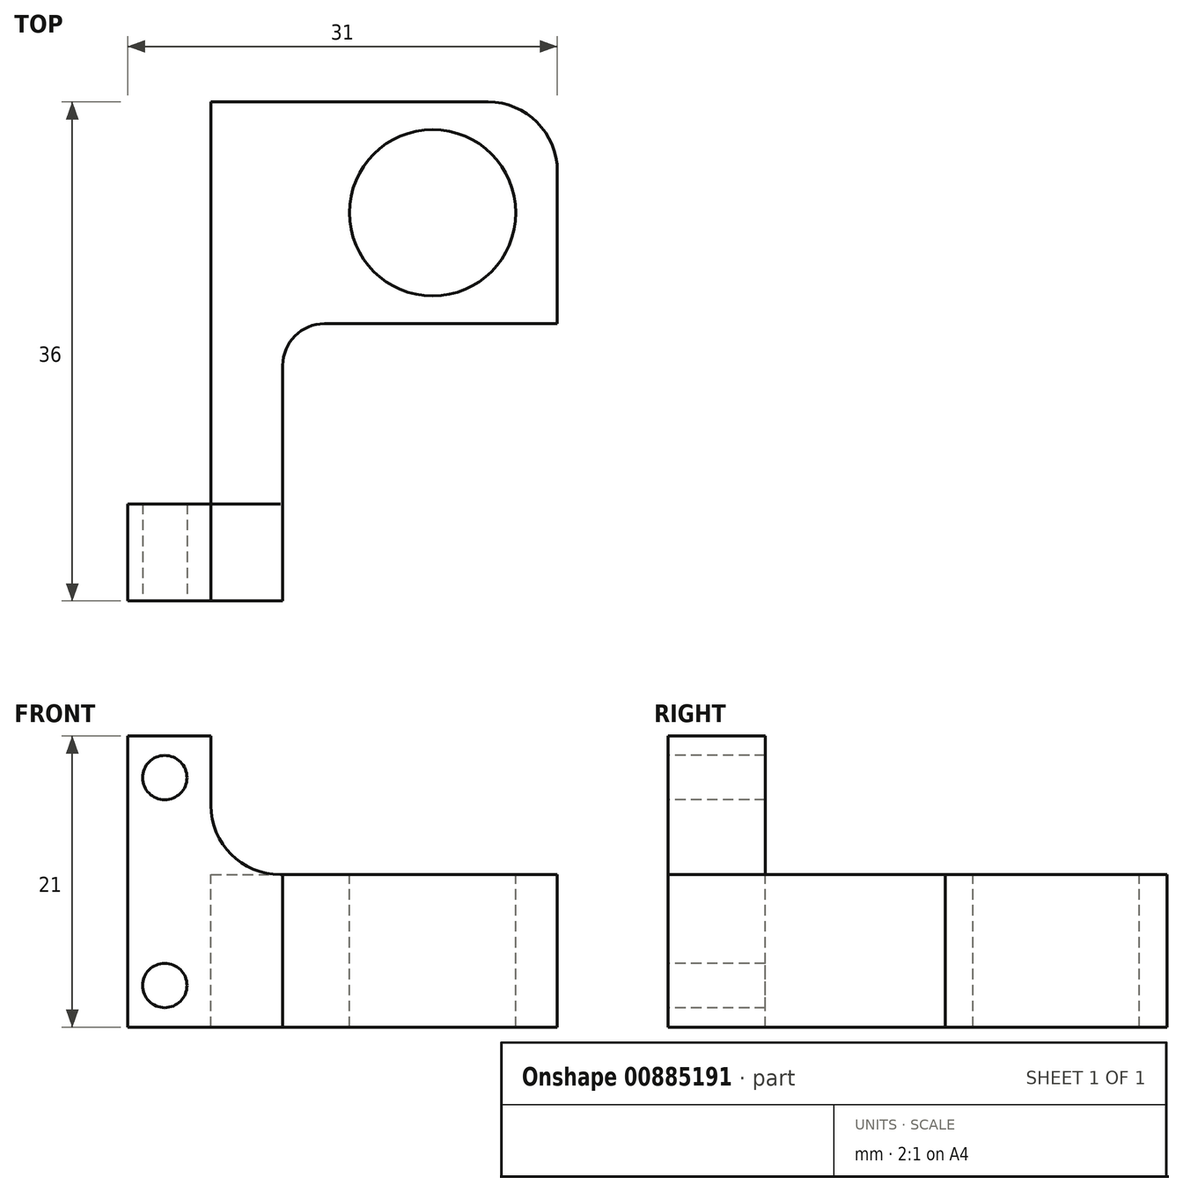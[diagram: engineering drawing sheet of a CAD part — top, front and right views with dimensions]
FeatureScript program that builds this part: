
annotation { "Feature Type Name" : "Feature", "Feature Type Description" : "" }
export const myFeature = defineFeature(function(context is Context, id is Id, definition is map)
    precondition{}
    {
        {
            var Q0;
            Q0=qCreatedBy(makeId("Top.planeOp"),FACE);
            var sketch = newSketch(context, id + "F0", { "sketchPlane" : qUnion([Q0])});
            skLineSegment(sketch, "E0.bottom", {"start": v(0, 0) * mm, "end": v(31, 0) * mm});
            skLineSegment(sketch, "E0.top", {"start": v(0, 36) * mm, "end": v(31, 36) * mm});
            skLineSegment(sketch, "E0.left", {"start": v(0, 0) * mm, "end": v(0, 36) * mm});
            skLineSegment(sketch, "E0.right", {"start": v(31, 0) * mm, "end": v(31, 36) * mm});
            skSolve(sketch);
        }
        {
            var Q0;
            Q0=qSketchRegion(id+"F0",true);
            extrude(context, id + "F1", {"entities" : qUnion([Q0]), "depth" : 4 * mm});
        }
        {
            var Q0;
            Q0=makeQuery(id+"F1.opExtrude","CAP_FACE",FACE,{"disambiguationData":[OSD([sQuery(id+"F0.wireOp",EDGE,"E0.bottom"),sQuery(id+"F0.wireOp",EDGE,"E0.top"),sQuery(id+"F0.wireOp",EDGE,"E0.left"),sQuery(id+"F0.wireOp",EDGE,"E0.right")])],"isStart":false});
            var sketch = newSketch(context, id + "F2", { "sketchPlane" : qUnion([Q0])});
            skCircle(sketch, "E1", {"center": v(22, 28) * mm, "radius": 6 * mm});
            skLineSegment(sketch, "E2.bottom", {"start": v(0, 36) * mm, "end": v(6, 36) * mm});
            skLineSegment(sketch, "E2.top", {"start": v(0, 7) * mm, "end": v(6, 7) * mm});
            skLineSegment(sketch, "E2.left", {"start": v(0, 36) * mm, "end": v(0, 7) * mm});
            skLineSegment(sketch, "E2.right", {"start": v(6, 36) * mm, "end": v(6, 7) * mm});
            skLineSegment(sketch, "E3.bottom", {"start": v(31, 0) * mm, "end": v(11.18, 0) * mm});
            skLineSegment(sketch, "E3.top", {"start": v(31, 20) * mm, "end": v(11.18, 20) * mm});
            skLineSegment(sketch, "E3.left", {"start": v(31, 0) * mm, "end": v(31, 20) * mm});
            skLineSegment(sketch, "E3.right", {"start": v(11.18, 0) * mm, "end": v(11.18, 20) * mm});
            skSolve(sketch);
        }
        {
            var Q0;
            Q0=qSketchRegion(id+"F2",true);
            extrude(context, id + "F3", {"entities" : qUnion([Q0]), "operationType" : NewBodyOperationType.REMOVE, "oppositeDirection" : true, "depth" : 25 * mm, "offsetDistance" : 25 * mm});
        }
        {
            var Q0;
            Q0=makeQuery(id+"F1.opExtrude","CAP_FACE",FACE,{"disambiguationData":[OSD([sQuery(id+"F0.wireOp",EDGE,"E0.bottom"),sQuery(id+"F0.wireOp",EDGE,"E0.top"),sQuery(id+"F0.wireOp",EDGE,"E0.left"),sQuery(id+"F0.wireOp",EDGE,"E0.right")])],"isStart":false});
            var sketch = newSketch(context, id + "F4", { "sketchPlane" : qUnion([Q0])});
            skLineSegment(sketch, "E4.bottom", {"start": v(0, 7) * mm, "end": v(6, 7) * mm});
            skLineSegment(sketch, "E4.top", {"start": v(0, 0) * mm, "end": v(6, 0) * mm});
            skLineSegment(sketch, "E4.left", {"start": v(0, 7) * mm, "end": v(0, 0) * mm});
            skLineSegment(sketch, "E4.right", {"start": v(6, 7) * mm, "end": v(6, 0) * mm});
            skSolve(sketch);
        }
        {
            var Q0;
            Q0=qSketchRegion(id+"F4",true);
            var Q1;
            {var subQ1=sQuery(id+"F4.wireOp",EDGE,"E4.right");Q1=makeQuery(id+"F4.imprint","IMPRINT",FACE,{"disambiguationData":[TD([[makeQuery(id+"F4.imprint","IMPRINT",EDGE,{"derivedFrom":subQ1}),1.0]])]});}
            extrude(context, id + "F5", {"entities" : qUnion([Q0, Q1]), "operationType" : NewBodyOperationType.ADD, "depth" : 7 * mm, "offsetDistance" : 25 * mm});
        }
        {
            var Q0;
            Q0=makeQuery(id+"F4.imprint","IMPRINT",FACE,{"disambiguationData":[TD([[makeQuery(id+"F4.imprint","IMPRINT",EDGE,{"derivedFrom":sQuery(id+"F4.wireOp",EDGE,"E4.bottom")}),-1.0]])]});
            extrude(context, id + "F6", {"entities" : qUnion([Q0]), "operationType" : NewBodyOperationType.ADD, "depth" : 17 * mm});
        }
        {
            var Q0;
            Q0=makeQuery(id+"F5.boolean.opBoolean","MERGE",FACE,{"derivedFrom":[makeQuery(id+"F1.opExtrude","SWEPT_FACE",FACE,{"disambiguationData":[OSD([sQuery(id+"F0.wireOp",EDGE,"E0.bottom")])]}),makeQuery(id+"F5.opExtrude","SWEPT_FACE",FACE,{"disambiguationData":[OSD([sQuery(id+"F4.wireOp",EDGE,"E4.top")])]})]});
            var sketch = newSketch(context, id + "F7", { "sketchPlane" : qUnion([Q0])});
            skLineSegment(sketch, "E5", {"start": v(2.68, 18) * mm, "end": v(2.68, 3) * mm});
            skCircle(sketch, "E6", {"center": v(2.68, 18) * mm, "radius": 1.6 * mm});
            skCircle(sketch, "E7", {"center": v(2.68, 3) * mm, "radius": 1.6 * mm});
            skSolve(sketch);
        }
        {
            var Q0;
            Q0=qSketchRegion(id+"F7",true);
            extrude(context, id + "F8", {"entities" : qUnion([Q0]), "operationType" : NewBodyOperationType.REMOVE, "oppositeDirection" : true, "depth" : 25 * mm});
        }
        {
            var Q0;
            Q0=makeQuery(id+"F1.opExtrude","SWEPT_EDGE",EDGE,{"disambiguationData":[OSD([sQuery(id+"F0.wireOp",EDGE,"E0.bottom"),sQuery(id+"F0.wireOp",EDGE,"E0.right")])]});
            var Q1;
            Q1=makeQuery(id+"F1.opExtrude","SWEPT_EDGE",EDGE,{"disambiguationData":[OSD([sQuery(id+"F0.wireOp",EDGE,"E0.top"),sQuery(id+"F0.wireOp",EDGE,"E0.right")])]});
            var Q2;
            Q2=makeQuery(id+"F3.boolean.opBoolean","COPY",EDGE,{"derivedFrom":makeQuery(id+"F3.opExtrude","SWEPT_EDGE",EDGE,{"disambiguationData":[OSD([sQuery(id+"F0.wireOp",EDGE,"E0.top"),sQuery(id+"F2.wireOp",EDGE,"E2.bottom"),sQuery(id+"F2.wireOp",EDGE,"E2.right")])]})});
            var Q3;
            Q3=makeQuery(id+"F3.boolean.opBoolean","COPY",EDGE,{"derivedFrom":makeQuery(id+"F3.opExtrude","SWEPT_EDGE",EDGE,{"disambiguationData":[OSD([sQuery(id+"F0.wireOp",EDGE,"E0.right"),sQuery(id+"F2.wireOp",EDGE,"E3.top"),sQuery(id+"F2.wireOp",EDGE,"E3.left")])]})});
            fillet(context, id + "F9", {"entities" : qUnion([Q0, Q1, Q2, Q3]), "radius" : 5 * mm, "tangentPropagation" : true, "allowEdgeOverflow" : false});
        }
        {
            var Q0;
            {var subQ0=sQuery(id+"F2.wireOp",EDGE,"E3.top");var subQ1=sQuery(id+"F2.wireOp",EDGE,"E3.right");Q0=makeQuery(id+"F5.boolean.opBoolean","MERGE",EDGE,{"derivedFrom":[makeQuery(id+"F3.boolean.opBoolean","COPY",EDGE,{"derivedFrom":makeQuery(id+"F3.opExtrude","SWEPT_EDGE",EDGE,{"disambiguationData":[OSD([subQ0,subQ1])]})}),makeQuery(id+"F5.opExtrude","SWEPT_EDGE",EDGE,{"disambiguationData":[OSD([subQ0,subQ1])]})]});}
            fillet(context, id + "F10", {"entities" : qUnion([Q0]), "radius" : 3 * mm, "tangentPropagation" : true, "allowEdgeOverflow" : false});
        }
        {
            var Q0;
            Q0=makeQuery(id+"F6.boolean.opBoolean","INTERSECT",EDGE,{"derivedFrom":[makeQuery(id+"F5.opExtrude","CAP_FACE",FACE,{"disambiguationData":[OSD([sQuery(id+"F0.wireOp",EDGE,"E0.bottom"),sQuery(id+"F0.wireOp",EDGE,"E0.top"),sQuery(id+"F0.wireOp",EDGE,"E0.right"),sQuery(id+"F2.wireOp",EDGE,"E1"),sQuery(id+"F2.wireOp",EDGE,"E2.right"),sQuery(id+"F2.wireOp",EDGE,"E3.top"),sQuery(id+"F2.wireOp",EDGE,"E3.right"),sQuery(id+"F4.wireOp",EDGE,"E4.bottom"),sQuery(id+"F4.wireOp",EDGE,"E4.top"),sQuery(id+"F4.wireOp",EDGE,"E4.left")])],"isStart":false}),makeQuery(id+"F6.opExtrude","SWEPT_FACE",FACE,{"disambiguationData":[OSD([sQuery(id+"F4.wireOp",EDGE,"E4.right")])]})]});
            fillet(context, id + "F11", {"entities" : qUnion([Q0]), "radius" : 5 * mm, "tangentPropagation" : true, "allowEdgeOverflow" : false});
        }
    });
